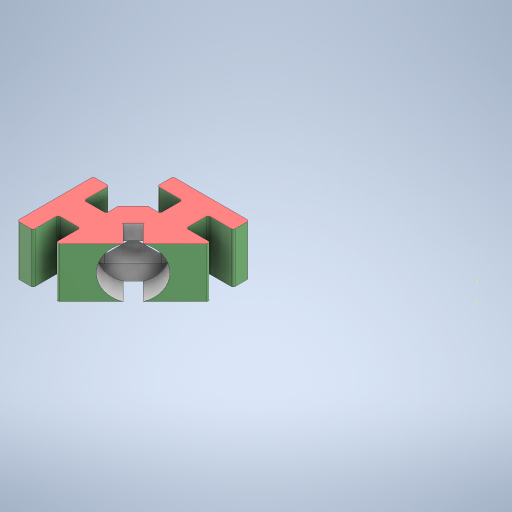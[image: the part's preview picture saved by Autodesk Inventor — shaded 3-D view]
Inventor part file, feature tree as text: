
AUTODESK INVENTOR PART (.ipt)
format: ipt  version: 2023 (Build 270158000, 158)  size: 357,888 bytes
history: native  units: in
note: dims shown in document units (in); Inventor stores cm internally (conversion verified against a paired STEP export)
features: sketch x6, other x4, extrude x3
ambient origin geometry x8: Origin, YZ Plane, XZ Plane, XY Plane, X Axis, Y Axis, Z Axis, Center Point
bodies: Body1 (feature_tree)
feature tree (13):
  other  "TmpPart3.ipt"
  sketch  "Sketch1"  dims[d0=0.3937in d1=0.2047in]
  extrude  "Extrusion1"  Depth=0.3937in
  sketch  "Sketch3"  dims[d5=0.0787in d6=0.126in d7=0.0in]
  sketch  "Sketch4"  dims[d8=0.0394in]
  extrude  "Extrusion2"  Depth=0.0787in
  extrude  "Extrusion3"  Depth=0.0787in TaperAngle=0.0deg
  other  "PLA2::TmpPart3.ipt"
  other  "TaggingFeature1"
  sketch  "Sketch2"  dims[d2=0.0984in d3=0.0in d4=0.0787in]
  sketch  "Sketch5"  dims[d9=90.0deg]
  sketch  "Sketch6"  dims[d10=0.0394in d11=180.0deg d12=45.0deg d13=0.0984in d14=0.0in d15=0.0197in d16=0.0344in]
  other  "PLA2"
